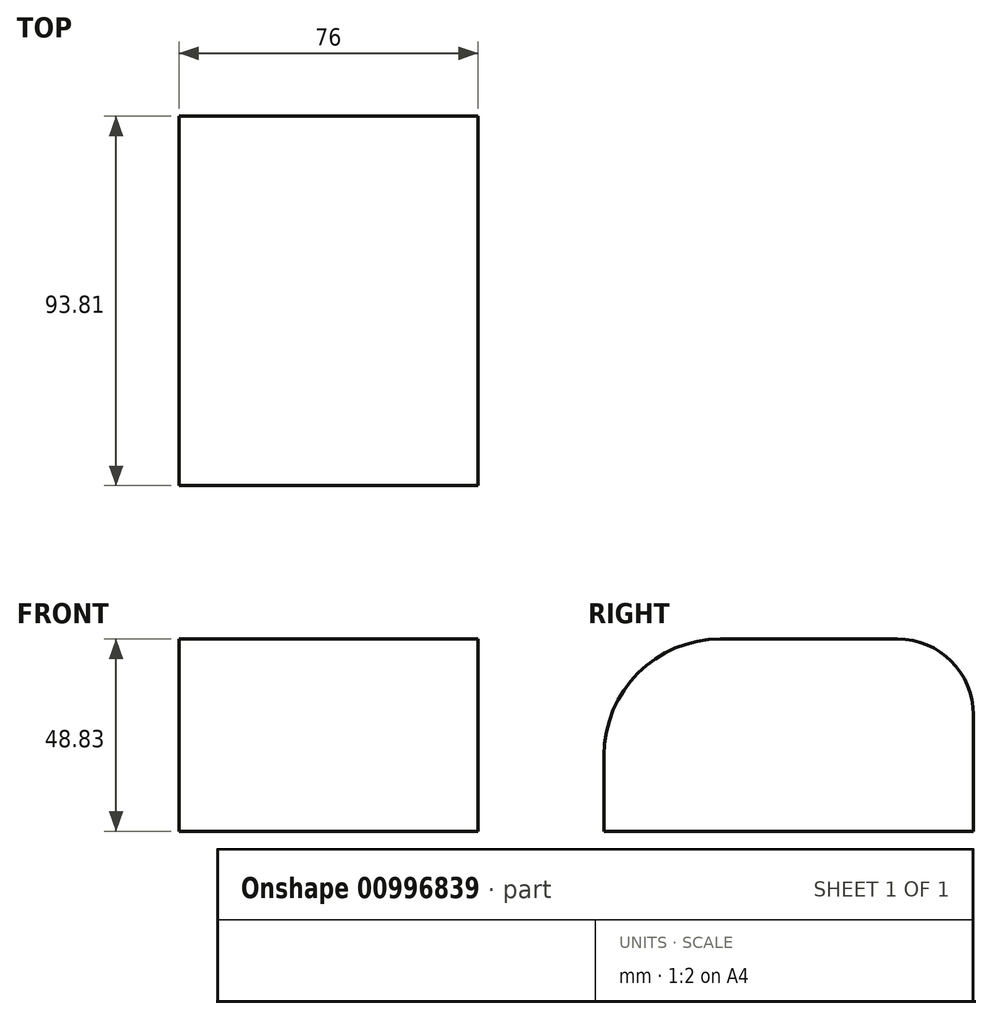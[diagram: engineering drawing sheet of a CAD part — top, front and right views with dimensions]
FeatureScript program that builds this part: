
annotation { "Feature Type Name" : "Feature", "Feature Type Description" : "" }
export const myFeature = defineFeature(function(context is Context, id is Id, definition is map)
    precondition{}
    {
        {
            var Q0;
            Q0=qCreatedBy(makeId("Front.planeOp"),FACE);
            var sketch = newSketch(context, id + "F0", { "sketchPlane" : qUnion([Q0])});
            skLineSegment(sketch, "E0.bottom", {"start": v(84.24, 67.98) * mm, "end": v(8.24, 67.98) * mm});
            skLineSegment(sketch, "E0.top", {"start": v(84.24, 19.15) * mm, "end": v(8.24, 19.15) * mm});
            skLineSegment(sketch, "E0.left", {"start": v(84.24, 67.98) * mm, "end": v(84.24, 19.15) * mm});
            skLineSegment(sketch, "E0.right", {"start": v(8.24, 67.98) * mm, "end": v(8.24, 19.15) * mm});
            skSolve(sketch);
        }
        {
            var Q0;
            Q0=makeQuery(id+"F0.imprint","IMPRINT",FACE,{"disambiguationData":[TD([[makeQuery(id+"F0.imprint","IMPRINT",EDGE,{"derivedFrom":sQuery(id+"F0.wireOp",EDGE,"E0.bottom")}),1.0]])]});
            extrude(context, id + "F1", {"entities" : qUnion([Q0]), "oppositeDirection" : true, "depth" : 93.81 * mm, "offsetDistance" : 25 * mm});
        }
        {
            var Q0;
            Q0=makeQuery(id+"F1.opExtrude","CAP_EDGE",EDGE,{"disambiguationData":[OSD([sQuery(id+"F0.wireOp",EDGE,"E0.bottom")])],"isStart":false});
            fillet(context, id + "F2", {"entities" : qUnion([Q0]), "radius" : 19.22 * mm, "tangentPropagation" : true, "allowEdgeOverflow" : false});
        }
        {
            var Q0;
            Q0=makeQuery(id+"F1.opExtrude","CAP_EDGE",EDGE,{"disambiguationData":[OSD([sQuery(id+"F0.wireOp",EDGE,"E0.bottom")])],"isStart":true});
            fillet(context, id + "F3", {"entities" : qUnion([Q0]), "radius" : 29.56 * mm, "tangentPropagation" : true, "allowEdgeOverflow" : false});
        }
    });
